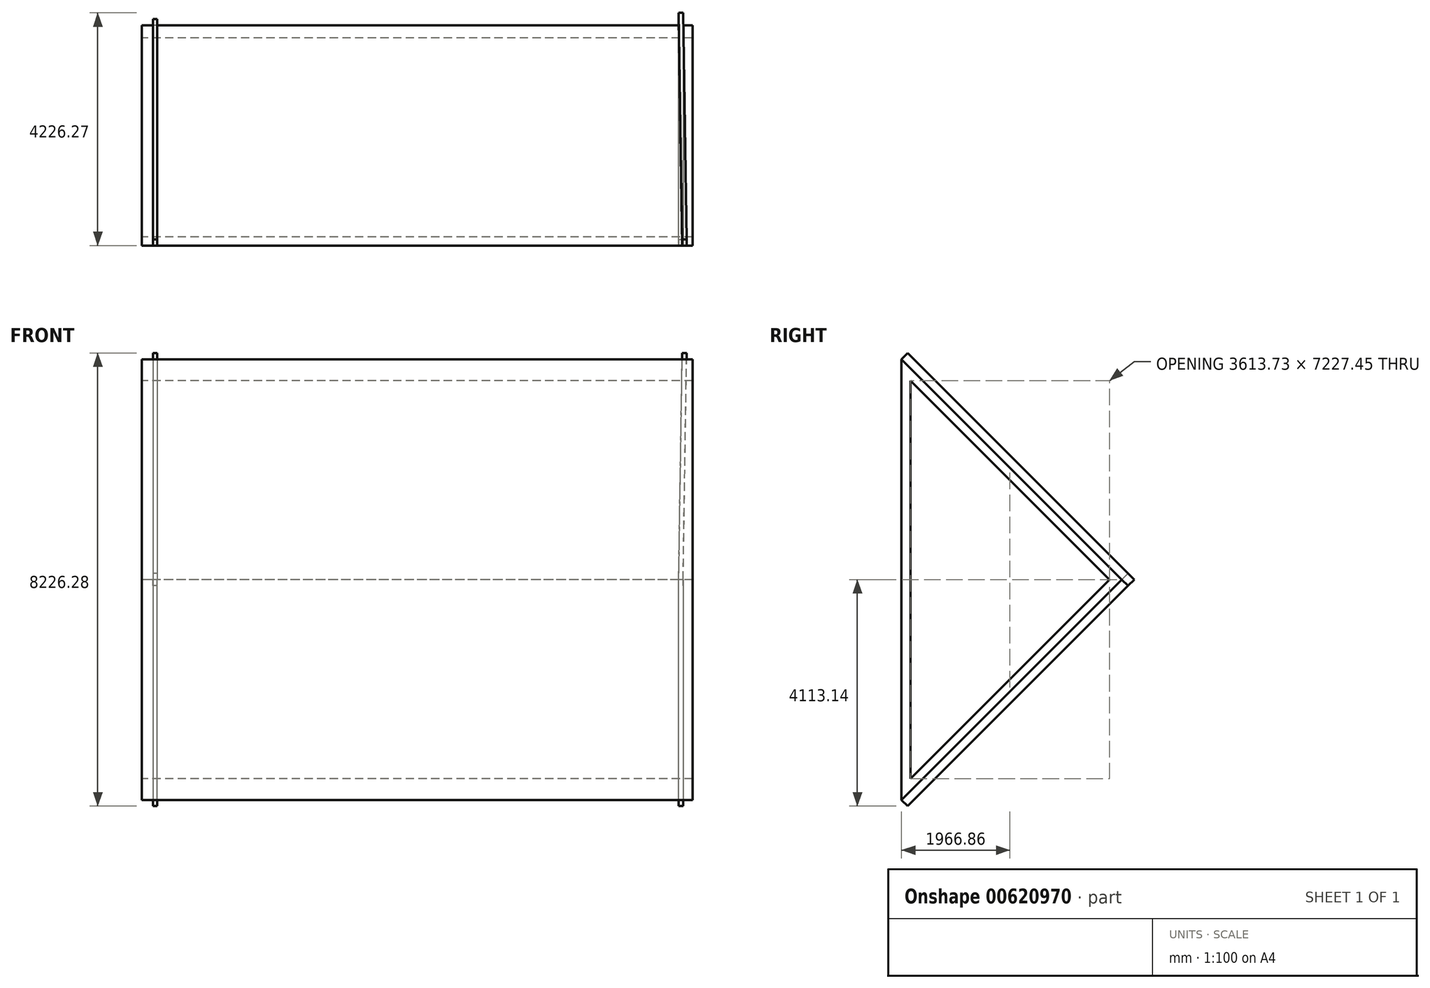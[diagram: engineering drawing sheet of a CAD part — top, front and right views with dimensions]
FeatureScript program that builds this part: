
annotation { "Feature Type Name" : "Feature", "Feature Type Description" : "" }
export const myFeature = defineFeature(function(context is Context, id is Id, definition is map)
    precondition{}
    {
        {
            var Q0;
            Q0=qCreatedBy(makeId("Front.planeOp"),FACE);
            var sketch = newSketch(context, id + "F0", { "sketchPlane" : qUnion([Q0])});
            skLineSegment(sketch, "E0.bottom", {"start": v(0, 0) * mm, "end": v(10000, 0) * mm});
            skLineSegment(sketch, "E0.top", {"start": v(0, 8000) * mm, "end": v(10000, 8000) * mm});
            skLineSegment(sketch, "E0.left", {"start": v(0, 0) * mm, "end": v(0, 8000) * mm});
            skLineSegment(sketch, "E0.right", {"start": v(10000, 0) * mm, "end": v(10000, 8000) * mm});
            skSolve(sketch);
        }
        {
            var Q0;
            Q0 = qSketchRegion(id + "F0", true);
            extrude(context, id + "F1", {"entities" : qUnion([Q0]), "depth" : 4000 * mm, "offsetDistance" : 25 * mm});
        }
        {
            var Q0;
            Q0=makeQuery(id+"F1.opExtrude","CAP_EDGE",EDGE,{"disambiguationData":[OSD([sQuery(id+"F0.wireOp",EDGE,"E0.bottom")])],"isStart":true});
            chamfer(context, id + "F2", {"entities" : qUnion([Q0]), "width" : 4000 * mm, "tangentPropagation" : true});
        }
        {
            var Q0;
            Q0=makeQuery(id+"F1.opExtrude","CAP_EDGE",EDGE,{"disambiguationData":[OSD([sQuery(id+"F0.wireOp",EDGE,"E0.top")])],"isStart":true});
            chamfer(context, id + "F3", {"entities" : qUnion([Q0]), "width" : 4000 * mm, "tangentPropagation" : true});
        }
        {
            var Q0;
            Q0=makeQuery(id+"F1.opExtrude","SWEPT_FACE",FACE,{"disambiguationData":[OSD([sQuery(id+"F0.wireOp",EDGE,"E0.left")])]});
            var sketch = newSketch(context, id + "F4", { "sketchPlane" : qUnion([Q0])});
            skLineSegment(sketch, "E1", {"start": v(3840, 7613.73) * mm, "end": v(226.27, 4000) * mm});
            skLineSegment(sketch, "E2", {"start": v(3840, 7613.73) * mm, "end": v(3840, 386.27) * mm});
            skLineSegment(sketch, "E3", {"start": v(226.27, 4000) * mm, "end": v(3840, 386.27) * mm});
            skSolve(sketch);
        }
        {
            var Q0;
            Q0=makeQuery(id+"F4.imprint","IMPRINT",FACE,{"disambiguationData":[TD([[makeQuery(id+"F4.imprint","IMPRINT",EDGE,{"derivedFrom":sQuery(id+"F4.wireOp",EDGE,"E1")}),1.0]])]});
            extrude(context, id + "F5", {"entities" : qUnion([Q0]), "operationType" : NewBodyOperationType.REMOVE, "oppositeDirection" : true, "depth" : 10000 * mm, "offsetDistance" : 25 * mm});
        }
        {
            var Q0;
            Q0=makeQuery(id+"F2.opChamfer","BLEND_FACE",FACE,{"disambiguationData":[OSD([sQuery(id+"F0.wireOp",EDGE,"E0.bottom")])]});
            var sketch = newSketch(context, id + "F6", { "sketchPlane" : qUnion([Q0])});
            skLineSegment(sketch, "E4", {"start": v(-10000, 2828.43) * mm, "end": v(-9825, 2828.43) * mm});
            skLineSegment(sketch, "E5", {"start": v(-9825, 2828.43) * mm, "end": v(-9825, -2828.43) * mm});
            skLineSegment(sketch, "E6", {"start": v(-9825, -2828.43) * mm, "end": v(-9745, -2828.43) * mm});
            skLineSegment(sketch, "E7", {"start": v(-9745, -2828.43) * mm, "end": v(-9745, 2828.71) * mm});
            skLineSegment(sketch, "E8", {"start": v(-9745, 2828.71) * mm, "end": v(-9825, 2828.43) * mm});
            skSolve(sketch);
        }
        {
            var Q0;
            {var subQ0=sQuery(id+"F6.wireOp",EDGE,"E5");Q0=makeQuery(id+"F6.imprint","IMPRINT",FACE,{"disambiguationData":[TD([[makeQuery(id+"F6.imprint","IMPRINT",EDGE,{"derivedFrom":subQ0}),1.0]])]});}
            extrude(context, id + "F7", {"entities" : qUnion([Q0]), "operationType" : NewBodyOperationType.ADD, "depth" : 160 * mm, "offsetDistance" : 25 * mm});
        }
        {
            var Q0;
            {var subQ0=sQuery(id+"F0.wireOp",EDGE,"E0.top");Q0=makeQuery(id+"F7.boolean.opBoolean","MERGE",FACE,{"derivedFrom":[makeQuery(id+"F3.opChamfer","BLEND_FACE",FACE,{"disambiguationData":[OSD([subQ0])]}),makeQuery(id+"F7.opExtrude","SWEPT_FACE",FACE,{"disambiguationData":[OSD([sQuery(id+"F0.wireOp",EDGE,"E0.bottom"),subQ0])]})]});}
            var sketch = newSketch(context, id + "F8", { "sketchPlane" : qUnion([Q0])});
            skLineSegment(sketch, "E9", {"start": v(-9825, 2668.43) * mm, "end": v(-9888.96, 8485.28) * mm});
            skLineSegment(sketch, "E10", {"start": v(-9745, 2668.43) * mm, "end": v(-9808.96, 8485.28) * mm});
            skLineSegment(sketch, "E11", {"start": v(-9825, 2668.43) * mm, "end": v(-9745, 2668.43) * mm});
            skLineSegment(sketch, "E12", {"start": v(-9888.96, 8485.28) * mm, "end": v(-9808.96, 8485.28) * mm});
            skLineSegment(sketch, "E13", {"start": v(-200, 8485.28) * mm, "end": v(-200, 2828.43) * mm});
            skLineSegment(sketch, "E14", {"start": v(-200, 2828.43) * mm, "end": v(-280, 2828.43) * mm});
            skLineSegment(sketch, "E15", {"start": v(-200, 8485.28) * mm, "end": v(-280, 8485.28) * mm});
            skLineSegment(sketch, "E16", {"start": v(-280, 8485.28) * mm, "end": v(-280, 2828.43) * mm});
            skSolve(sketch);
        }
        {
            var Q0;
            Q0=makeQuery(id+"F8.imprint","IMPRINT",FACE,{"disambiguationData":[TD([[makeQuery(id+"F8.imprint","IMPRINT",EDGE,{"derivedFrom":sQuery(id+"F8.wireOp",EDGE,"E10")}),1.0]])]});
            extrude(context, id + "F9", {"entities" : qUnion([Q0]), "operationType" : NewBodyOperationType.ADD, "depth" : 160 * mm, "offsetDistance" : 25 * mm});
        }
        {
            var Q0;
            {var subQ0=sQuery(id+"F0.wireOp",EDGE,"E0.left");var subQ2=sQuery(id+"F0.wireOp",EDGE,"E0.bottom");Q0=makeQuery(id+"F7.boolean.opBoolean","SPLIT",FACE,{"disambiguationData":[TD([makeQuery(id+"F1.opExtrude","SWEPT_FACE",FACE,{"disambiguationData":[OSD([subQ0])]})])],"derivedFrom":makeQuery(id+"F2.opChamfer","BLEND_FACE",FACE,{"disambiguationData":[OSD([subQ2])]})});}
            var sketch = newSketch(context, id + "F10", { "sketchPlane" : qUnion([Q0])});
            skLineSegment(sketch, "E17", {"start": v(-200, 2828.43) * mm, "end": v(-200, -2828.43) * mm});
            skLineSegment(sketch, "E18", {"start": v(-200, -2828.43) * mm, "end": v(-280, -2828.43) * mm});
            skLineSegment(sketch, "E19", {"start": v(-280, -2828.43) * mm, "end": v(-280, 2828.43) * mm});
            skLineSegment(sketch, "E20", {"start": v(-280, 2828.43) * mm, "end": v(-200, 2828.43) * mm});
            skSolve(sketch);
        }
        {
            var Q0;
            Q0 = qSketchRegion(id + "F10", true);
            extrude(context, id + "F11", {"entities" : qUnion([Q0]), "operationType" : NewBodyOperationType.ADD, "depth" : 160 * mm, "offsetDistance" : 25 * mm});
        }
        {
            var Q0;
            Q0 = qSketchRegion(id + "F8", true);
            extrude(context, id + "F12", {"entities" : qUnion([Q0]), "operationType" : NewBodyOperationType.ADD, "depth" : 160 * mm, "offsetDistance" : 25 * mm});
        }
    });
